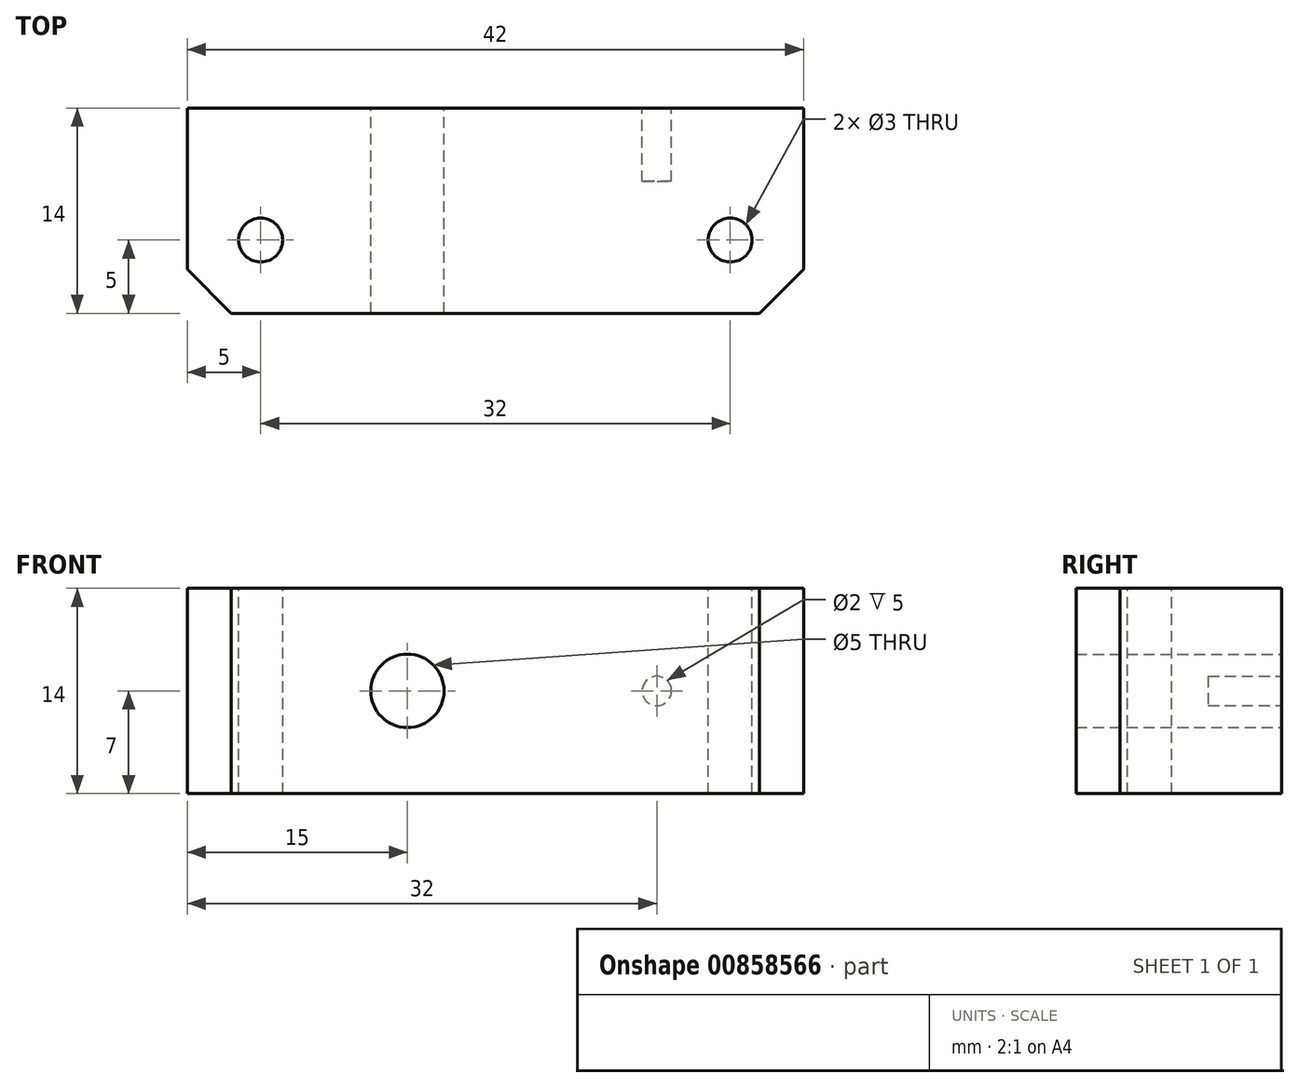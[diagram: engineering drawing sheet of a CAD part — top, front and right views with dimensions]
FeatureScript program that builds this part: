
annotation { "Feature Type Name" : "Feature", "Feature Type Description" : "" }
export const myFeature = defineFeature(function(context is Context, id is Id, definition is map)
    precondition{}
    {
        {
            var Q0;
            Q0=qCreatedBy(makeId("Top.planeOp"),FACE);
            var sketch = newSketch(context, id + "F0", { "sketchPlane" : qUnion([Q0])});
            skLineSegment(sketch, "E0.bottom", {"start": v(0, 0) * mm, "end": v(42, 0) * mm});
            skLineSegment(sketch, "E0.top", {"start": v(0, -14) * mm, "end": v(42, -14) * mm});
            skLineSegment(sketch, "E0.left", {"start": v(0, 0) * mm, "end": v(0, -14) * mm});
            skLineSegment(sketch, "E0.right", {"start": v(42, 0) * mm, "end": v(42, -14) * mm});
            skSolve(sketch);
        }
        {
            var Q0;
            Q0=makeQuery(id+"F0.imprint","IMPRINT",FACE,{"disambiguationData":[TD([[makeQuery(id+"F0.imprint","IMPRINT",EDGE,{"derivedFrom":sQuery(id+"F0.wireOp",EDGE,"E0.bottom")}),-1.0]])]});
            extrude(context, id + "F1", {"entities" : qUnion([Q0]), "depth" : 14 * mm, "offsetDistance" : 25 * mm});
        }
        {
            var Q0;
            Q0=makeQuery(id+"F1.opExtrude","CAP_FACE",FACE,{"disambiguationData":[OSD([sQuery(id+"F0.wireOp",EDGE,"E0.bottom"),sQuery(id+"F0.wireOp",EDGE,"E0.top"),sQuery(id+"F0.wireOp",EDGE,"E0.left"),sQuery(id+"F0.wireOp",EDGE,"E0.right")])],"isStart":false});
            var sketch = newSketch(context, id + "F2", { "sketchPlane" : qUnion([Q0])});
            skLineSegment(sketch, "E1", {"start": v(0, -14) * mm, "end": v(5, -14) * mm});
            skLineSegment(sketch, "E2", {"start": v(5, -14) * mm, "end": v(5, -9) * mm});
            skLineSegment(sketch, "E3", {"start": v(42, -14) * mm, "end": v(37, -14) * mm});
            skLineSegment(sketch, "E4", {"start": v(37, -14) * mm, "end": v(37, -9) * mm});
            skCircle(sketch, "E5", {"center": v(5, -9) * mm, "radius": 1.5 * mm});
            skCircle(sketch, "E6", {"center": v(37, -9) * mm, "radius": 1.5 * mm});
            skSolve(sketch);
        }
        {
            var Q0;
            Q0 = qSketchRegion(id + "F2", true);
            extrude(context, id + "F3", {"entities" : qUnion([Q0]), "operationType" : NewBodyOperationType.REMOVE, "oppositeDirection" : true, "depth" : 25 * mm, "offsetDistance" : 25 * mm});
        }
        {
            var Q0;
            Q0=makeQuery(id+"F1.opExtrude","SWEPT_FACE",FACE,{"disambiguationData":[OSD([sQuery(id+"F0.wireOp",EDGE,"E0.bottom")])]});
            var sketch = newSketch(context, id + "F4", { "sketchPlane" : qUnion([Q0])});
            skLineSegment(sketch, "E7", {"start": v(-42, 7) * mm, "end": v(-32, 7) * mm});
            skCircle(sketch, "E8", {"center": v(-32, 7) * mm, "radius": 1 * mm});
            skSolve(sketch);
        }
        {
            var Q0;
            Q0 = qSketchRegion(id + "F4", true);
            extrude(context, id + "F5", {"entities" : qUnion([Q0]), "operationType" : NewBodyOperationType.REMOVE, "oppositeDirection" : true, "depth" : 5 * mm, "offsetDistance" : 25 * mm});
        }
        {
            var Q0;
            Q0=makeQuery(id+"F1.opExtrude","SWEPT_FACE",FACE,{"disambiguationData":[OSD([sQuery(id+"F0.wireOp",EDGE,"E0.bottom")])]});
            var sketch = newSketch(context, id + "F6", { "sketchPlane" : qUnion([Q0])});
            skLineSegment(sketch, "E9", {"start": v(0, 7) * mm, "end": v(-15, 7) * mm});
            skCircle(sketch, "E10", {"center": v(-15, 7) * mm, "radius": 2.5 * mm});
            skSolve(sketch);
        }
        {
            var Q0;
            Q0 = qSketchRegion(id + "F6", true);
            extrude(context, id + "F7", {"entities" : qUnion([Q0]), "operationType" : NewBodyOperationType.REMOVE, "oppositeDirection" : true, "depth" : 25 * mm, "offsetDistance" : 25 * mm});
        }
        {
            var Q0;
            Q0=makeQuery(id+"F1.opExtrude","SWEPT_EDGE",EDGE,{"disambiguationData":[OSD([sQuery(id+"F0.wireOp",EDGE,"E0.top"),sQuery(id+"F0.wireOp",EDGE,"E0.left")])]});
            var Q1;
            Q1=makeQuery(id+"F1.opExtrude","SWEPT_EDGE",EDGE,{"disambiguationData":[OSD([sQuery(id+"F0.wireOp",EDGE,"E0.top"),sQuery(id+"F0.wireOp",EDGE,"E0.right")])]});
            chamfer(context, id + "F8", {"entities" : qUnion([Q0, Q1]), "width" : 3 * mm, "tangentPropagation" : true});
        }
    });
